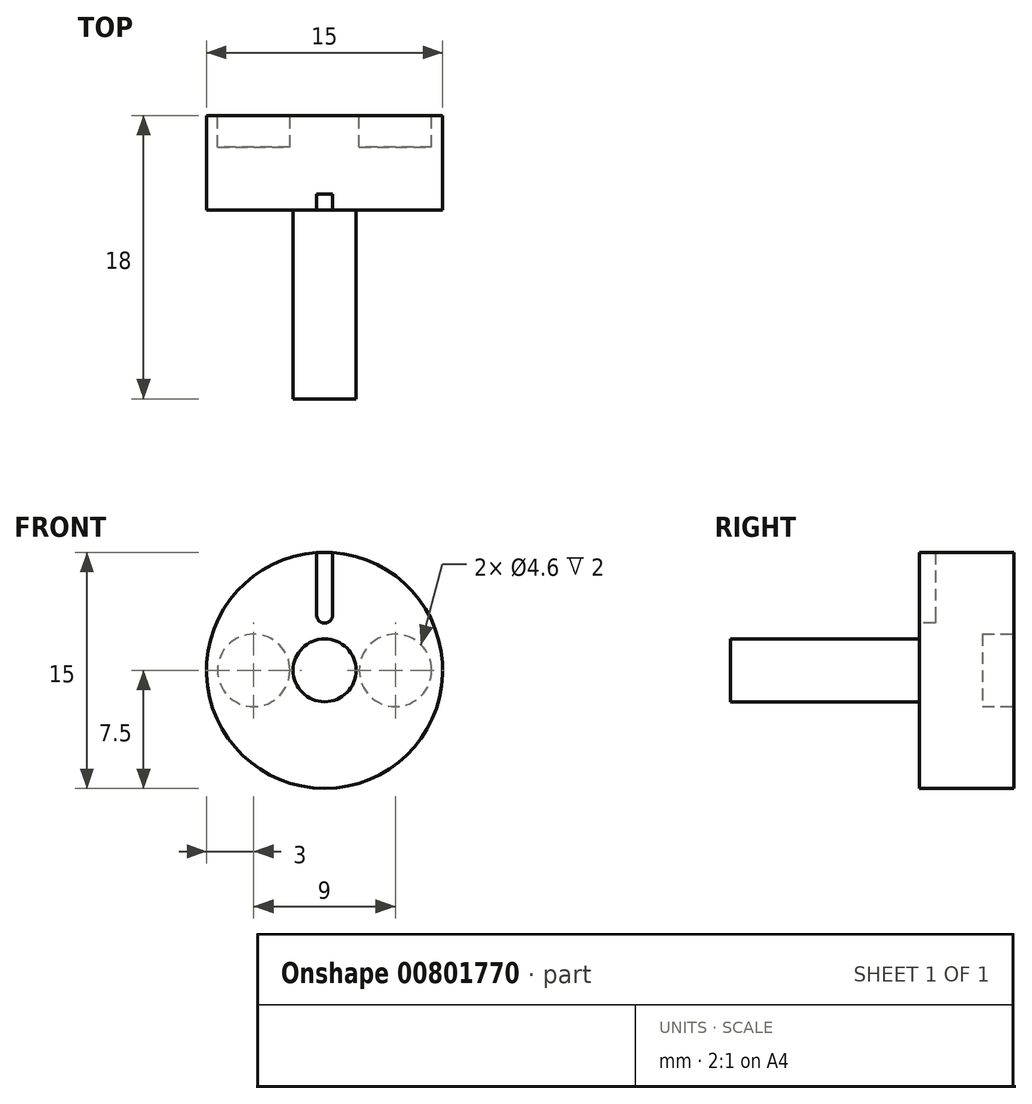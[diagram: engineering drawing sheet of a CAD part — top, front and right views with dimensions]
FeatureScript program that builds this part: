
annotation { "Feature Type Name" : "Feature", "Feature Type Description" : "" }
export const myFeature = defineFeature(function(context is Context, id is Id, definition is map)
    precondition{}
    {
        {
            var Q0;
            Q0=qCreatedBy(makeId("Front.planeOp"),FACE);
            var sketch = newSketch(context, id + "F0", { "sketchPlane" : qUnion([Q0])});
            skCircle(sketch, "E0", {"center": v(0, 0) * mm, "radius": 7.5 * mm});
            skSolve(sketch);
        }
        {
            var Q0;
            Q0=qSketchRegion(id+"F0",true);
            extrude(context, id + "F1", {"entities" : qUnion([Q0]), "depth" : 6 * mm, "offsetDistance" : 25 * mm});
        }
        {
            var Q0;
            Q0=makeQuery(id+"F1.opExtrude","CAP_FACE",FACE,{"disambiguationData":[OSD([sQuery(id+"F0.wireOp",EDGE,"E0")])],"isStart":false});
            var sketch = newSketch(context, id + "F2", { "sketchPlane" : qUnion([Q0])});
            skCircle(sketch, "E1", {"center": v(0, 0) * mm, "radius": 2 * mm});
            skSolve(sketch);
        }
        {
            var Q0;
            Q0=qSketchRegion(id+"F2",true);
            extrude(context, id + "F3", {"entities" : qUnion([Q0]), "operationType" : NewBodyOperationType.ADD, "depth" : 12 * mm, "offsetDistance" : 25 * mm});
        }
        {
            var Q0;
            Q0=makeQuery(id+"F1.opExtrude","CAP_FACE",FACE,{"disambiguationData":[OSD([sQuery(id+"F0.wireOp",EDGE,"E0")])],"isStart":true});
            var sketch = newSketch(context, id + "F4", { "sketchPlane" : qUnion([Q0])});
            skCircle(sketch, "E2", {"center": v(-4.5, 0) * mm, "radius": 2.3 * mm});
            skCircle(sketch, "E3", {"center": v(4.5, 0) * mm, "radius": 2.3 * mm});
            skSolve(sketch);
        }
        {
            var Q0;
            Q0=qSketchRegion(id+"F4",true);
            extrude(context, id + "F5", {"entities" : qUnion([Q0]), "operationType" : NewBodyOperationType.REMOVE, "oppositeDirection" : true, "depth" : 2 * mm, "offsetDistance" : 25 * mm});
        }
        {
            var Q0;
            Q0=makeQuery(id+"F1.opExtrude","CAP_FACE",FACE,{"disambiguationData":[OSD([sQuery(id+"F0.wireOp",EDGE,"E0")])],"isStart":false});
            var sketch = newSketch(context, id + "F6", { "sketchPlane" : qUnion([Q0])});
            skLineSegment(sketch, "E4", {"start": v(0.5, 7.48) * mm, "end": v(0.5, 3.5) * mm});
            skLineSegment(sketch, "E5.MirrorCS", {"start": v(-0.5, 7.48) * mm, "end": v(-0.5, 3.5) * mm});
            skArc(sketch, "E6", {"start": v(-0.5, 3.5) * mm, "mid": v(0, 3) * mm, "end": v(0.5, 3.5) * mm});
            skSolve(sketch);
        }
        {
            var Q0;
            {var subQ0=sQuery(id+"F6.wireOp",EDGE,"E4");Q0=makeQuery(id+"F6.imprint","IMPRINT",FACE,{"disambiguationData":[TD([[makeQuery(id+"F6.imprint","IMPRINT",EDGE,{"derivedFrom":subQ0}),-1.0]])]});}
            extrude(context, id + "F7", {"entities" : qUnion([Q0]), "operationType" : NewBodyOperationType.REMOVE, "oppositeDirection" : true, "depth" : 1 * mm, "offsetDistance" : 25 * mm});
        }
    });
